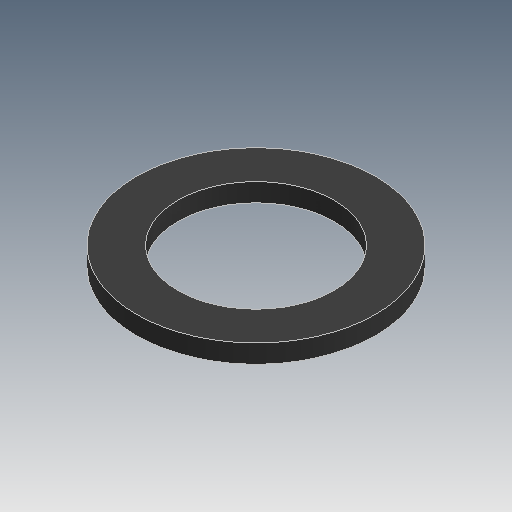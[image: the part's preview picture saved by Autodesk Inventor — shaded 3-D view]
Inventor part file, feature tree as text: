
AUTODESK INVENTOR PART (.ipt)
format: ipt  version: 2025 (Build 290162000, 162)  size: 290,304 bytes
history: native  units: mm
features: extrude x1, sketch x1
ambient origin geometry x8: Origin, YZ Plane, XZ Plane, XY Plane, X Axis, Y Axis, Z Axis, Center Point
bodies: 实体1 (feature_tree)
feature tree (2):
  extrude  "拉伸1"  Depth=2.0mm
  sketch  "草图1"  dims[d0=26.0mm d1=17.0mm d2=2.0mm d3=0.0mm]
